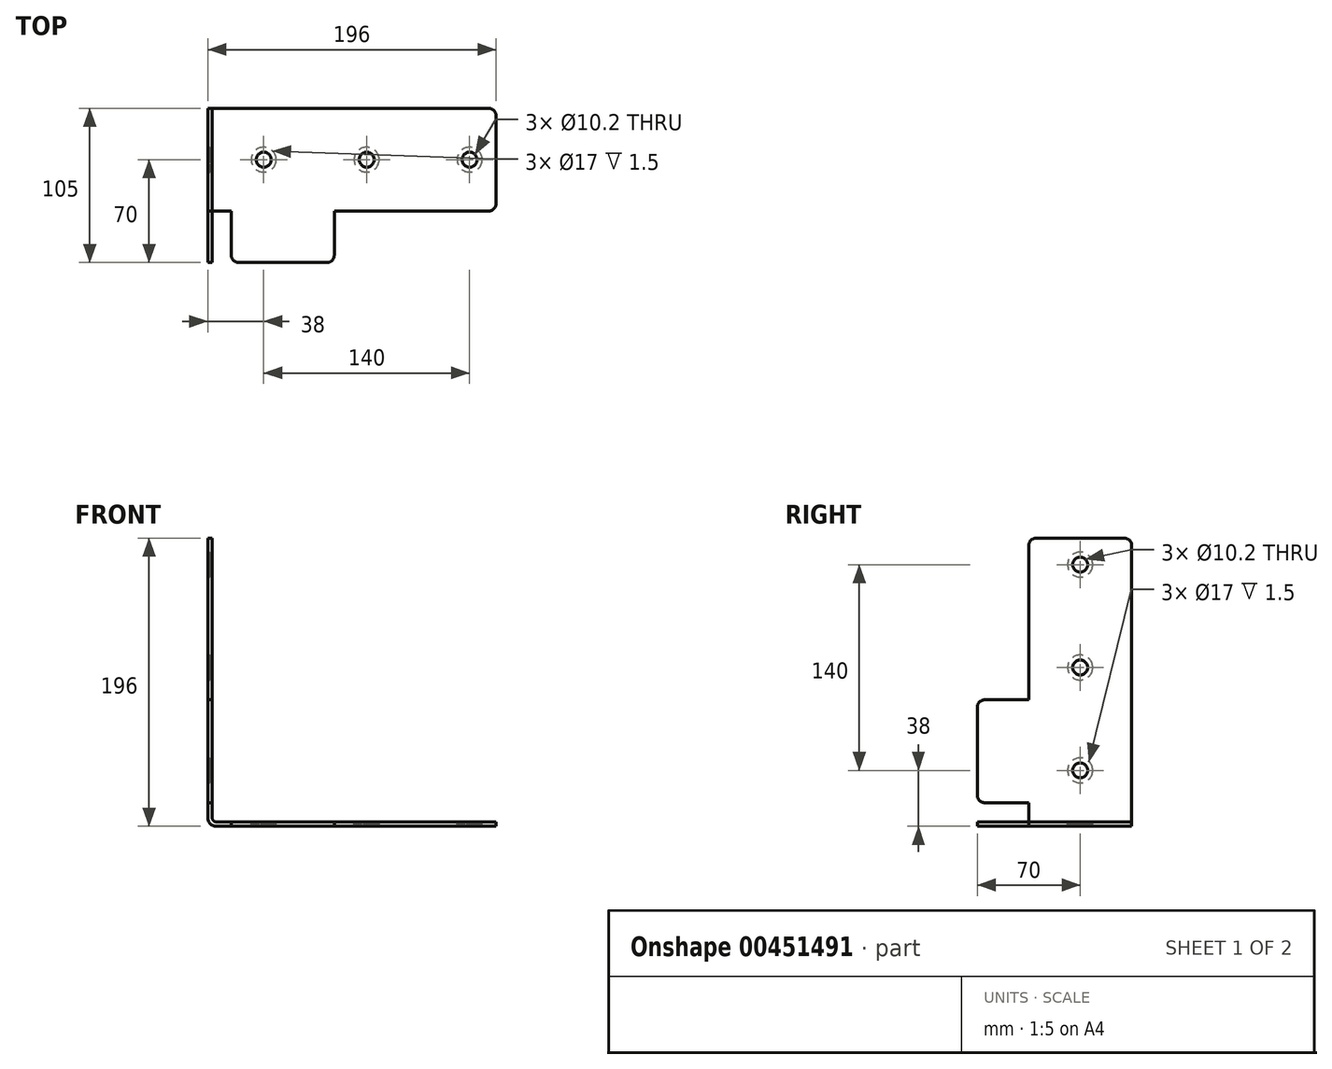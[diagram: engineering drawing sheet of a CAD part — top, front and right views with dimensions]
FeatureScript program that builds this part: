
annotation { "Feature Type Name" : "Feature", "Feature Type Description" : "" }
export const myFeature = defineFeature(function(context is Context, id is Id, definition is map)
    precondition{}
    {
        {
            var Q0;
            Q0=qCreatedBy(makeId("Right.planeOp"),FACE);
            var Q1;
            Q1=qCreatedBy(makeId("Top.planeOp"),FACE);
            cPlane(context, id + "F0", {"entities" : qUnion([Q0, Q1]), "cplaneType" : CPlaneType.MID_PLANE, "offset" : 25 * mm, "width" : 150 * mm, "height" : 150 * mm});
        }
        {
            var Q0;
            Q0=qCreatedBy(makeId("Front.planeOp"),FACE);
            var sketch = newSketch(context, id + "F1", { "sketchPlane" : qUnion([Q0])});
            skLineSegment(sketch, "E0", {"start": v(0, 196) * mm, "end": v(0, 0) * mm});
            skLineSegment(sketch, "E1", {"start": v(0, 0) * mm, "end": v(196, 0) * mm});
            skLineSegment(sketch, "E2.0", {"start": v(3, 3) * mm, "end": v(196, 3) * mm});
            skLineSegment(sketch, "E2.1", {"start": v(3, 196) * mm, "end": v(3, 3) * mm});
            skLineSegment(sketch, "E3", {"start": v(196, 0) * mm, "end": v(196, 3) * mm});
            skLineSegment(sketch, "E4", {"start": v(0, 196) * mm, "end": v(3, 196) * mm});
            skSolve(sketch);
        }
        {
            var Q0;
            Q0=qSketchRegion(id+"F1",true);
            extrude(context, id + "F2", {"entities" : qUnion([Q0]), "oppositeDirection" : true, "depth" : 70 * mm});
        }
        {
            var Q0;
            Q0=makeQuery(id+"F2.opExtrude","SWEPT_EDGE",EDGE,{"disambiguationData":[OSD([sQuery(id+"F1.wireOp",EDGE,"E0"),sQuery(id+"F1.wireOp",EDGE,"E1")])]});
            fillet(context, id + "F3", {"entities" : qUnion([Q0]), "radius" : 5.6 * mm, "tangentPropagation" : true, "allowEdgeOverflow" : false});
        }
        {
            var Q0;
            Q0=makeQuery(id+"F2.opExtrude","SWEPT_EDGE",EDGE,{"disambiguationData":[OSD([sQuery(id+"F1.wireOp",EDGE,"E2.0"),sQuery(id+"F1.wireOp",EDGE,"E2.1")])]});
            fillet(context, id + "F4", {"entities" : qUnion([Q0]), "radius" : 2.6 * mm, "tangentPropagation" : true, "allowEdgeOverflow" : false});
        }
        {
            var Q0;
            Q0=makeQuery(id+"F2.opExtrude","CAP_FACE",FACE,{"disambiguationData":[OSD([sQuery(id+"F1.wireOp",EDGE,"E0"),sQuery(id+"F1.wireOp",EDGE,"E1"),sQuery(id+"F1.wireOp",EDGE,"E2.0"),sQuery(id+"F1.wireOp",EDGE,"E2.1"),sQuery(id+"F1.wireOp",EDGE,"E3"),sQuery(id+"F1.wireOp",EDGE,"E4")])],"isStart":true});
            var sketch = newSketch(context, id + "F5", { "sketchPlane" : qUnion([Q0])});
            skLineSegment(sketch, "E5", {"start": v(16, 3) * mm, "end": v(86, 3) * mm});
            skLineSegment(sketch, "E6", {"start": v(86, 3) * mm, "end": v(86, 0) * mm});
            skLineSegment(sketch, "E7", {"start": v(86, 0) * mm, "end": v(16, 0) * mm});
            skLineSegment(sketch, "E8", {"start": v(16, 3) * mm, "end": v(16, 0) * mm});
            skLineSegment(sketch, "E9.MirrorCS", {"start": v(3, 16) * mm, "end": v(0, 16) * mm});
            skLineSegment(sketch, "E10.MirrorCS", {"start": v(3, 16) * mm, "end": v(3, 86) * mm});
            skLineSegment(sketch, "E11.MirrorCS", {"start": v(0, 86) * mm, "end": v(0, 16) * mm});
            skLineSegment(sketch, "E12.MirrorCS", {"start": v(3, 86) * mm, "end": v(0, 86) * mm});
            skSolve(sketch);
        }
        {
            var Q0;
            Q0=qSketchRegion(id+"F5",true);
            extrude(context, id + "F6", {"entities" : qUnion([Q0]), "operationType" : NewBodyOperationType.ADD, "depth" : 35 * mm});
        }
        {
            var Q0;
            Q0=makeQuery(id+"F6.opExtrude","CAP_EDGE",EDGE,{"disambiguationData":[OSD([sQuery(id+"F5.wireOp",EDGE,"E8")])],"isStart":true});
            var Q1;
            Q1=makeQuery(id+"F6.opExtrude","CAP_EDGE",EDGE,{"disambiguationData":[OSD([sQuery(id+"F5.wireOp",EDGE,"E8")])],"isStart":false});
            var Q2;
            Q2=makeQuery(id+"F6.opExtrude","CAP_EDGE",EDGE,{"disambiguationData":[OSD([sQuery(id+"F5.wireOp",EDGE,"E6")])],"isStart":false});
            var Q3;
            Q3=makeQuery(id+"F6.opExtrude","CAP_EDGE",EDGE,{"disambiguationData":[OSD([sQuery(id+"F5.wireOp",EDGE,"E6")])],"isStart":true});
            var Q4;
            Q4=makeQuery(id+"F6.opExtrude","CAP_EDGE",EDGE,{"disambiguationData":[OSD([sQuery(id+"F5.wireOp",EDGE,"E9.MirrorCS")])],"isStart":false});
            var Q5;
            Q5=makeQuery(id+"F6.opExtrude","CAP_EDGE",EDGE,{"disambiguationData":[OSD([sQuery(id+"F5.wireOp",EDGE,"E12.MirrorCS")])],"isStart":false});
            var Q6;
            Q6=makeQuery(id+"F6.opExtrude","CAP_EDGE",EDGE,{"disambiguationData":[OSD([sQuery(id+"F5.wireOp",EDGE,"E9.MirrorCS")])],"isStart":true});
            var Q7;
            Q7=makeQuery(id+"F6.opExtrude","CAP_EDGE",EDGE,{"disambiguationData":[OSD([sQuery(id+"F5.wireOp",EDGE,"E12.MirrorCS")])],"isStart":true});
            var Q8;
            Q8=makeQuery(id+"F2.opExtrude","CAP_EDGE",EDGE,{"disambiguationData":[OSD([sQuery(id+"F1.wireOp",EDGE,"E4")])],"isStart":true});
            var Q9;
            Q9=makeQuery(id+"F2.opExtrude","CAP_EDGE",EDGE,{"disambiguationData":[OSD([sQuery(id+"F1.wireOp",EDGE,"E4")])],"isStart":false});
            var Q10;
            Q10=makeQuery(id+"F2.opExtrude","CAP_EDGE",EDGE,{"disambiguationData":[OSD([sQuery(id+"F1.wireOp",EDGE,"E3")])],"isStart":false});
            var Q11;
            Q11=makeQuery(id+"F2.opExtrude","CAP_EDGE",EDGE,{"disambiguationData":[OSD([sQuery(id+"F1.wireOp",EDGE,"E3")])],"isStart":true});
            fillet(context, id + "F7", {"entities" : qUnion([Q0, Q1, Q2, Q3, Q4, Q5, Q6, Q7, Q8, Q9, Q10, Q11]), "radius" : 5 * mm, "tangentPropagation" : true, "allowEdgeOverflow" : false});
        }
        {
            var Q0;
            Q0=makeQuery(id+"F6.boolean.opBoolean","MERGE",FACE,{"derivedFrom":[makeQuery(id+"F2.opExtrude","SWEPT_FACE",FACE,{"disambiguationData":[OSD([sQuery(id+"F1.wireOp",EDGE,"E1")])]}),makeQuery(id+"F6.opExtrude","SWEPT_FACE",FACE,{"disambiguationData":[OSD([sQuery(id+"F5.wireOp",EDGE,"E7")])]})]});
            var sketch = newSketch(context, id + "F8", { "sketchPlane" : qUnion([Q0])});
            skPoint(sketch, "E13", {"position": v(38, -35) * mm});
            skPoint(sketch, "E14", {"position": v(108, -35) * mm});
            skPoint(sketch, "E15", {"position": v(178, -35) * mm});
            skSolve(sketch);
        }
        {
            var Q0;
            Q0=makeQuery(id+"F6.boolean.opBoolean","MERGE",FACE,{"derivedFrom":[makeQuery(id+"F2.opExtrude","SWEPT_FACE",FACE,{"disambiguationData":[OSD([sQuery(id+"F1.wireOp",EDGE,"E0")])]}),makeQuery(id+"F6.opExtrude","SWEPT_FACE",FACE,{"disambiguationData":[OSD([sQuery(id+"F5.wireOp",EDGE,"E11.MirrorCS")])]})]});
            var sketch = newSketch(context, id + "F9", { "sketchPlane" : qUnion([Q0])});
            skPoint(sketch, "E16", {"position": v(-35, 178) * mm});
            skPoint(sketch, "E17", {"position": v(-35, 108) * mm});
            skPoint(sketch, "E18", {"position": v(-35, 38) * mm});
            skSolve(sketch);
        }
        {
            var Q0;
            Q0=sQuery(id+"F8.wireOp",VERTEX,"E13");
            var Q1;
            Q1=sQuery(id+"F8.wireOp",VERTEX,"E14");
            var Q2;
            Q2=sQuery(id+"F8.wireOp",VERTEX,"E15");
            var Q3;
            Q3=sQuery(id+"F9.wireOp",VERTEX,"E16");
            var Q4;
            Q4=sQuery(id+"F9.wireOp",VERTEX,"E17");
            var Q5;
            Q5=sQuery(id+"F9.wireOp",VERTEX,"E18");
            var Q6;
            Q6=makeQuery(id+"F2.opExtrude","SWEPT_BODY",BODY,{"disambiguationData":[OSD([sQuery(id+"F1.wireOp",EDGE,"E0"),sQuery(id+"F1.wireOp",EDGE,"E1"),sQuery(id+"F1.wireOp",EDGE,"E2.0"),sQuery(id+"F1.wireOp",EDGE,"E2.1"),sQuery(id+"F1.wireOp",EDGE,"E3"),sQuery(id+"F1.wireOp",EDGE,"E4")])]});
            hole(context, id + "F10", {"style" : HoleStyle.C_BORE, "endStyle" : HoleEndStyle.THROUGH, "holeDiameter" : 10.2 * mm, "cBoreDiameter" : 17 * mm, "cBoreDepth" : 1.5 * mm, "locations" : qUnion([Q0, Q1, Q2, Q3, Q4, Q5]), "scope" : qUnion([Q6]), "isTappedThrough" : true, "startStyle" : HoleStartStyle.PART});
        }
    });
